# Revit family: Maxlogic Пожарные извещатели
name_source: partatom
category: Fire Alarm Devices
units: mm (PartAtom-declared; Revit-internal decimal feet)

## family parameters
Cut with Voids When Loaded = No
Host = Face
Maintain Annotation Orientation = Yes
OmniClass Number = 23.85.30.21
OmniClass Title = Environmental Detection/Registration
Part Type = Normal
Room Calculation Point = No
Round Connector Dimension = Use Diameter
Shared = No

## types (10) — shared parameters
Manufacturer = Mavili Elektronik Ticaret A.Ş.
Model = Maxlogic
URL = https://www.mavili.com.tr
Адрес №1 = Şerifali Mahallesi Kutup Sokak No:27/1-2-4 Ümraniye TR-34775 İSTANBUL
Вторичный материал = Пластмассовый
Гарантийный срок = Года
Гарантийный срок запчастей = 2
Гарантия срока службы = 2
Главный Материал = Белый пластмассовый PC/ABS
Инструкция по установке = https://mavilielektronik.com
Монтажный комплект для установки извещателя в подвесной потолок = ML-0150
Монтажный короб для установки извещателя с поверхностной прокладкой кабеля = ML-0121
Номер телефона = (+)90 216 466 45 05
Номер факса = (+)90 216 466 45 10
Номинальная высота = 106 мм
Номинальная глубина = 51 мм
Номинальная ширина = 106 мм
Рабочая Температура = (-10°C) - (+50°C)
Рабочее напряжение (по умолчанию) = 26 В Пост. ток
Совместимые базы для монтажа = ML-0140
Совместимые базы для монтажа 2 = ML-0141
Цвет = Белый
zero-valued in all types: Cost, Default Elevation

## per-type parameters (varying)
| type | Description | Isı halka | Multi sensör halka | Вес | Выход индикации | Диапазон рабочего напряжения | Код продукта | Монтажная поверхность | Настройка адреса устройства | Номер позы общественных работ | Производительность кода | Радиус обнаружения |
| Maxlogic Неадресный извещатель дымовой оптико-электронный | Неадресный извещатель дымовой оптико-электронный | No | No | 140 гр | MG-4000 | 10-30В Пост. ток | ML-2110 | Потолочная |  | 832-106 | EN 54-7 | 6,2 m |
| Maxlogic Адресный извещатель дымовой | Адресный извещатель дымовой | No | No | 100 гр | MG-4000.A | 18-33В Пост. ток | ML-1110 | Настенная | Модульная адресация | 833-500 | EN 54-7 | 6,2 m |
| Maxlogic Адресный Извещатель дымовой с изолятором КЗ | Адресный Извещатель дымовой с изолятором КЗ | No | No | 100 гр | MG-4000.A | 18-33В Пост. ток | ML-1110.SCI | Потолочная | Модульная адресация | 833-501 | EN 54-7 / EN 54-17 | 6,2 m |
| Maxlogic Неадресный максимальный тепловой извещатель | Неадресный максимальный тепловой извещатель | Yes | No | 135 гр | MG-4000 | 10-30В Пост. ток | ML-2120 | Потолочная |  | 832-102 | EN 54-5 | 4,5 m |
| Неадресный максимально-дифференциальный тепловой извещатель | Неадресный максимально-дифференциальный тепловой извещатель | Yes | No | 135 гр | MG-4000 | 10-30В Пост. ток | ML-2130 | Потолочная |  | 832-103 | EN 54-5 | 4,5 m |
| Maxlogic  Адресный извещатель тепловой | Адресный извещатель тепловой | Yes | No | 95 гр | MG-4000.A | 18-33В Пост. ток | ML-1130 | Потолочная | Модульная адресация | 833-520 | EN 54-5 | 4,5 m |
| Maxlogic Адресный извещатель тепловой с изолятором КЗ | Адресный извещатель тепловой с изолятором КЗ | Yes | No | 95 гр | MG-4000.A | 18-33В Пост. ток | ML-1130.SCI | Потолочная | Модульная адресация | 833-521 | EN 54-5 / EN 54-17 | 4,5 m |
| Maxlogic Неадресный извещатель комбинированый (Дым + Тепла) | Неадресный извещатель комбинированый (Дым + Тепла) | Yes | Yes | 141 гр | MG-4000 | 10-30В Пост. ток | ML-2140 | Потолочная |  | 832-109 | EN 54-5 / EN 54-7 | 4,5 m |
| Maxlogic Адресный извещатель комбинированый (Дым + Тепла) | Адресный извещатель комбинированый (Дым + Тепла) | Yes | Yes | 100 гр | MG-4000.A | 18-33В Пост. ток | ML-1140 | Потолочная | Модульная адресация | 833-530 | EN 54-5 / EN 54-7 / EN 54-17 | 4,5 m |
| Maxlogic Адресный извещатель комбинированый (Дым + Тепла) с изолятором КЗ | Адресный извещатель комбинированый (Дым + Тепла) с изолятором КЗ | Yes | Yes | 100 гр | MG-4000.A | 18-33В Пост. ток | ML-1140.SCI | Потолочная | Модульная адресация | 833-531 | EN 54-5 / EN 54-7 / EN 54-17 | 4,5 m |

## geometry (parser evidence)
native form markers: Sweep x1
no freeform markers — native parametric forms only
